# Revit family: NLRS_33_GM_FB_TC_STORAX_vloerluik_S-50EX_BCB
name_source: partatom
category: Generic Models
revit_build: Autodesk Revit 2015 (Build: 20140223_1515(x64)
units: mm (PartAtom-declared; Revit-internal decimal feet)

## types (1)
- NLRS_33_GM_FB_TC_STORAX_vloerluik_S-50EX_BCB
    Default Elevation = 0 mm  [stored 0 ft]
    Manufacturer = Storax
    Model = S50EX
    URL = https://www.storax.nl
    bediening = handmatig
    belasting kg/m2 = 200
    brandwerend 60 min = No
    cilinderslot = No
    code productgroep = LUI
    conservering = brut
    dagmaatbreedte = 760 mm
    dagmaatlengte = 915 mm
    deurblad = vlak
    false = No
    garantietermijn in jaren = 10
    gewicht = 54.00 kg
    hoogte = 305 mm
    loopslot = No
    materiaal = bcb_aluminium
    modeler = Bouwconnect
    omranding dakopstand = Yes
    omranding hoekprofiel = No
    omranding waterafvoerend = No
    omschrijving = explosieluik
    ontgrendelingsmechanisme = Yes
    openingshoek = 90.00°
    plaatdikte = 2 mm  [stored 0.00656168 ft]
    productgroep = Dakluiken
    scharnierend = Yes
    thermische onderbreking = No
    true = Yes
    uitwendige_breedte = 938 mm
    uitwendige_lengte = 1093 mm
    veersysteem = No
    waterdicht = Yes

note: [stored X ft] marks values corroborated as IEEE doubles in the binary element streams (Revit-internal decimal feet)

## geometry (parser evidence)
native form markers: Blend x768, Sweep x7
no freeform markers — native parametric forms only
